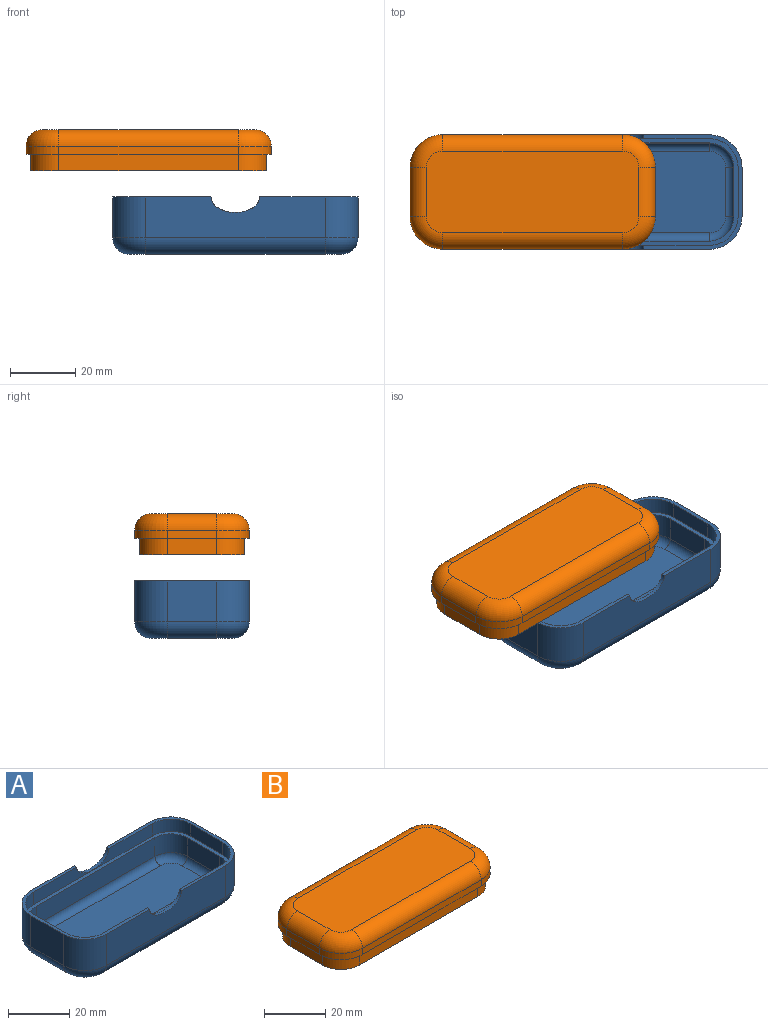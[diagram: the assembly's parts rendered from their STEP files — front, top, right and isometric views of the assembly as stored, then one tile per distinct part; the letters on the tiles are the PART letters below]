
ASSEMBLY  parts=2 mates=1
PART A: 47 faces, bbox 76.6x36.6x17.5 mm
  f0: plane 72.6x32.6mm, normal (0,0,1), area 248.6mm2, adj f10,f11,f12,f13,f14,f15,f16,f17
  f1: plane 65x25mm, normal (0,0,1), area 1603.5mm2, adj f2,f3,f4,f5,f6,f7,f8,f9
  f2: cylinder r=2.5mm len=15mm, axis (0,1,0), area 58.9mm2, adj f1,f3,f9,f17
  f3: torus R=5mm, axis (0,0,1), area 40.7mm2, adj f1,f2,f4,f16
  f4: cylinder r=2.5mm len=55mm, axis (-1,0,0), area 216mm2, adj f1,f3,f5,f15
  f5: torus R=5mm, axis (0,0,1), area 40.7mm2, adj f1,f4,f6,f14
  f6: cylinder r=2.5mm len=15mm, axis (0,-1,0), area 58.9mm2, adj f1,f5,f7,f13
  f7: torus R=5mm, axis (0,0,1), area 40.7mm2, adj f1,f6,f8,f12
  f8: cylinder r=2.5mm len=55mm, axis (1,0,0), area 216mm2, adj f1,f7,f9,f11
  f9: torus R=5mm, axis (0,0,1), area 40.7mm2, adj f1,f2,f8,f10
  f10: cylinder r=7.5mm len=7.5mm, axis (0,0,-1), area 88.4mm2, adj f0,f9,f11,f17
  f11: plane 55x7.5mm, normal (0,1,0), area 412.5mm2, adj f0,f8,f10,f12
  f12: cylinder r=7.5mm len=7.5mm, axis (0,0,-1), area 88.4mm2, adj f0,f7,f11,f13
  f13: plane 15x7.5mm, normal (1,0,0), area 112.5mm2, adj f0,f6,f12,f14
  f14: cylinder r=7.5mm len=7.5mm, axis (0,0,-1), area 88.4mm2, adj f0,f5,f13,f15
  f15: plane 55x7.5mm, normal (0,-1,0), area 412.5mm2, adj f0,f4,f14,f16
  f16: cylinder r=7.5mm len=7.5mm, axis (0,0,-1), area 88.4mm2, adj f0,f3,f15,f17
  f17: plane 15x7.5mm, normal (-1,0,0), area 112.5mm2, adj f0,f2,f10,f16
  f18: cylinder r=8.8mm len=8.8mm, axis (0,0,1), area 69.1mm2, adj f0,f19,f25,f43
  f19: plane 15x5mm, normal (-1,0,0), area 75mm2, adj f0,f18,f20,f43
  f20: cylinder r=8.8mm len=8.8mm, axis (0,0,1), area 69.1mm2, adj f0,f19,f21,f43
  f21: plane 55x5mm, normal (0,-1,0), area 219.4mm2, adj f0,f20,f22,f43,f44,f46
  f22: cylinder r=8.8mm len=8.8mm, axis (0,0,1), area 69.1mm2, adj f0,f21,f23,f44
  f23: plane 15x5mm, normal (1,0,0), area 75mm2, adj f0,f22,f24,f44
  f24: cylinder r=8.8mm len=8.8mm, axis (0,0,1), area 69.1mm2, adj f0,f23,f25,f44
  f25: plane 55x5mm, normal (0,1,0), area 219.4mm2, adj f0,f18,f24,f43,f44,f45
  f26: plane 65x25mm, normal (0,0,-1), area 1603.5mm2, adj f27,f28,f29,f30,f31,f32,f33,f34
  f27: torus R=5mm, axis (0,0,1), area 101mm2, adj f26,f28,f34,f35
  f28: cylinder r=5mm len=15mm, axis (0,1,0), area 117.8mm2, adj f26,f27,f29,f36
  f29: torus R=5mm, axis (0,0,1), area 101mm2, adj f26,f28,f30,f37
  f30: cylinder r=5mm len=55mm, axis (1,0,0), area 432mm2, adj f26,f29,f31,f38
  f31: torus R=5mm, axis (0,0,1), area 101mm2, adj f26,f30,f32,f39
  f32: cylinder r=5mm len=15mm, axis (0,-1,0), area 117.8mm2, adj f26,f31,f33,f40
  f33: torus R=5mm, axis (0,0,1), area 101mm2, adj f26,f32,f34,f41
  f34: cylinder r=5mm len=55mm, axis (-1,0,0), area 432mm2, adj f26,f27,f33,f42
  f35: cylinder r=10mm len=12.5mm, axis (0,0,-1), area 196.3mm2, adj f27,f36,f42,f43
  f36: plane 15x12.5mm, normal (1,0,0), area 187.5mm2, adj f28,f35,f37,f43
  f37: cylinder r=10mm len=12.5mm, axis (0,0,-1), area 196.3mm2, adj f29,f36,f38,f43
  f38: plane 55x12.5mm, normal (0,-1,0), area 631.9mm2, adj f30,f37,f39,f43,f44,f45
  f39: cylinder r=10mm len=12.5mm, axis (0,0,-1), area 196.3mm2, adj f31,f38,f40,f44
  f40: plane 15x12.5mm, normal (-1,0,0), area 187.5mm2, adj f32,f39,f41,f44
  f41: cylinder r=10mm len=12.5mm, axis (0,0,-1), area 196.3mm2, adj f33,f40,f42,f44
  f42: plane 55x12.5mm, normal (0,1,0), area 631.9mm2, adj f34,f35,f41,f43,f44,f46
  f43: plane 35x30.05mm, normal (0,0,1), area 101.6mm2, adj f18,f19,f20,f21,f25,f35,f36,f37
  f44: plane 35x30.05mm, normal (0,0,1), area 101.6mm2, adj f21,f22,f23,f24,f25,f38,f39,f40
  f45: extruded ~14.91x4.75mm, area 23.3mm2, adj f25,f38,f43,f44
  f46: extruded ~14.91x4.75mm, area 23.3mm2, adj f21,f42,f43,f44
PART B: 44 faces, bbox 76.6x36.6x12.5 mm
  f0: plane 15x7.5mm, normal (-1,0,0), area 112.5mm2, adj f1,f7,f13,f17
  f1: cylinder r=7.5mm len=7.5mm, axis (0,0,-1), area 88.4mm2, adj f0,f2,f11,f17
  f2: plane 55x7.5mm, normal (0,-1,0), area 412.5mm2, adj f1,f3,f9,f17
  f3: cylinder r=7.5mm len=7.5mm, axis (0,0,-1), area 88.4mm2, adj f2,f4,f10,f17
  f4: plane 15x7.5mm, normal (1,0,0), area 112.5mm2, adj f3,f5,f12,f17
  f5: cylinder r=7.5mm len=7.5mm, axis (0,0,-1), area 88.4mm2, adj f4,f6,f14,f17
  f6: plane 55x7.5mm, normal (0,1,0), area 412.5mm2, adj f5,f7,f16,f17
  f7: cylinder r=7.5mm len=7.5mm, axis (0,0,-1), area 88.4mm2, adj f0,f6,f15,f17
  f8: plane 65x25mm, normal (0,0,-1), area 1603.5mm2, adj f9,f10,f11,f12,f13,f14,f15,f16
  f9: cylinder r=2.5mm len=55mm, axis (1,0,0), area 216mm2, adj f2,f8,f10,f11
  f10: torus R=5mm, axis (0,0,1), area 40.7mm2, adj f3,f8,f9,f12
  f11: torus R=5mm, axis (0,0,1), area 40.7mm2, adj f1,f8,f9,f13
  f12: cylinder r=2.5mm len=15mm, axis (0,1,0), area 58.9mm2, adj f4,f8,f10,f14
  f13: cylinder r=2.5mm len=15mm, axis (0,-1,0), area 58.9mm2, adj f0,f8,f11,f15
  f14: torus R=5mm, axis (0,0,1), area 40.7mm2, adj f5,f8,f12,f16
  f15: torus R=5mm, axis (0,0,1), area 40.7mm2, adj f7,f8,f13,f16
  f16: cylinder r=2.5mm len=55mm, axis (-1,0,0), area 216mm2, adj f6,f8,f14,f15
  f17: plane 72x32mm, normal (0,0,-1), area 190.3mm2, adj f0,f1,f2,f3,f4,f5,f6,f7
  f18: plane 75x35mm, normal (0,0,-1), area 297.2mm2, adj f19,f20,f21,f22,f23,f24,f25,f26
  f19: plane 55x5mm, normal (0,-1,0), area 275mm2, adj f17,f18,f20,f26
  f20: cylinder r=8.5mm len=8.5mm, axis (0,0,1), area 66.8mm2, adj f17,f18,f19,f21
  f21: plane 15x5mm, normal (1,0,0), area 75mm2, adj f17,f18,f20,f22
  f22: cylinder r=8.5mm len=8.5mm, axis (0,0,1), area 66.8mm2, adj f17,f18,f21,f23
  f23: plane 55x5mm, normal (0,1,0), area 275mm2, adj f17,f18,f22,f24
  f24: cylinder r=8.5mm len=8.5mm, axis (0,0,1), area 66.8mm2, adj f17,f18,f23,f25
  f25: plane 15x5mm, normal (-1,0,0), area 75mm2, adj f17,f18,f24,f26
  f26: cylinder r=8.5mm len=8.5mm, axis (0,0,1), area 66.8mm2, adj f17,f18,f19,f25
  f27: plane 65x25mm, normal (0,0,1), area 1603.5mm2, adj f28,f29,f30,f31,f32,f33,f34,f35
  f28: torus R=5mm, axis (0,0,1), area 101mm2, adj f27,f29,f35,f43
  f29: cylinder r=5mm len=55mm, axis (-1,0,0), area 432mm2, adj f27,f28,f30,f42
  f30: torus R=5mm, axis (0,0,1), area 101mm2, adj f27,f29,f31,f41
  f31: cylinder r=5mm len=15mm, axis (0,1,0), area 117.8mm2, adj f27,f30,f32,f40
  f32: torus R=5mm, axis (0,0,1), area 101mm2, adj f27,f31,f33,f39
  f33: cylinder r=5mm len=55mm, axis (1,0,0), area 432mm2, adj f27,f32,f34,f38
  f34: torus R=5mm, axis (0,0,1), area 101mm2, adj f27,f33,f35,f37
  f35: cylinder r=5mm len=15mm, axis (0,-1,0), area 117.8mm2, adj f27,f28,f34,f36
  f36: plane 15x2.5mm, normal (1,0,0), area 37.5mm2, adj f18,f35,f37,f43
  f37: cylinder r=10mm len=10mm, axis (0,0,-1), area 39.3mm2, adj f18,f34,f36,f38
  f38: plane 55x2.5mm, normal (0,1,0), area 137.5mm2, adj f18,f33,f37,f39
  f39: cylinder r=10mm len=10mm, axis (0,0,-1), area 39.3mm2, adj f18,f32,f38,f40
  f40: plane 15x2.5mm, normal (-1,0,0), area 37.5mm2, adj f18,f31,f39,f41
  f41: cylinder r=10mm len=10mm, axis (0,0,-1), area 39.3mm2, adj f18,f30,f40,f42
  f42: plane 55x2.5mm, normal (0,-1,0), area 137.5mm2, adj f18,f29,f41,f43
  f43: cylinder r=10mm len=10mm, axis (0,0,-1), area 39.3mm2, adj f18,f28,f36,f42
PLACE A at identity fixed
PLACE B rot(axis=(1,0,0),0deg) t=(-26.51,0,13.05)mm
MATE slider A.f44 <-> B.f18  axis (0,0,1) through (-17.99,2.5,5)mm
